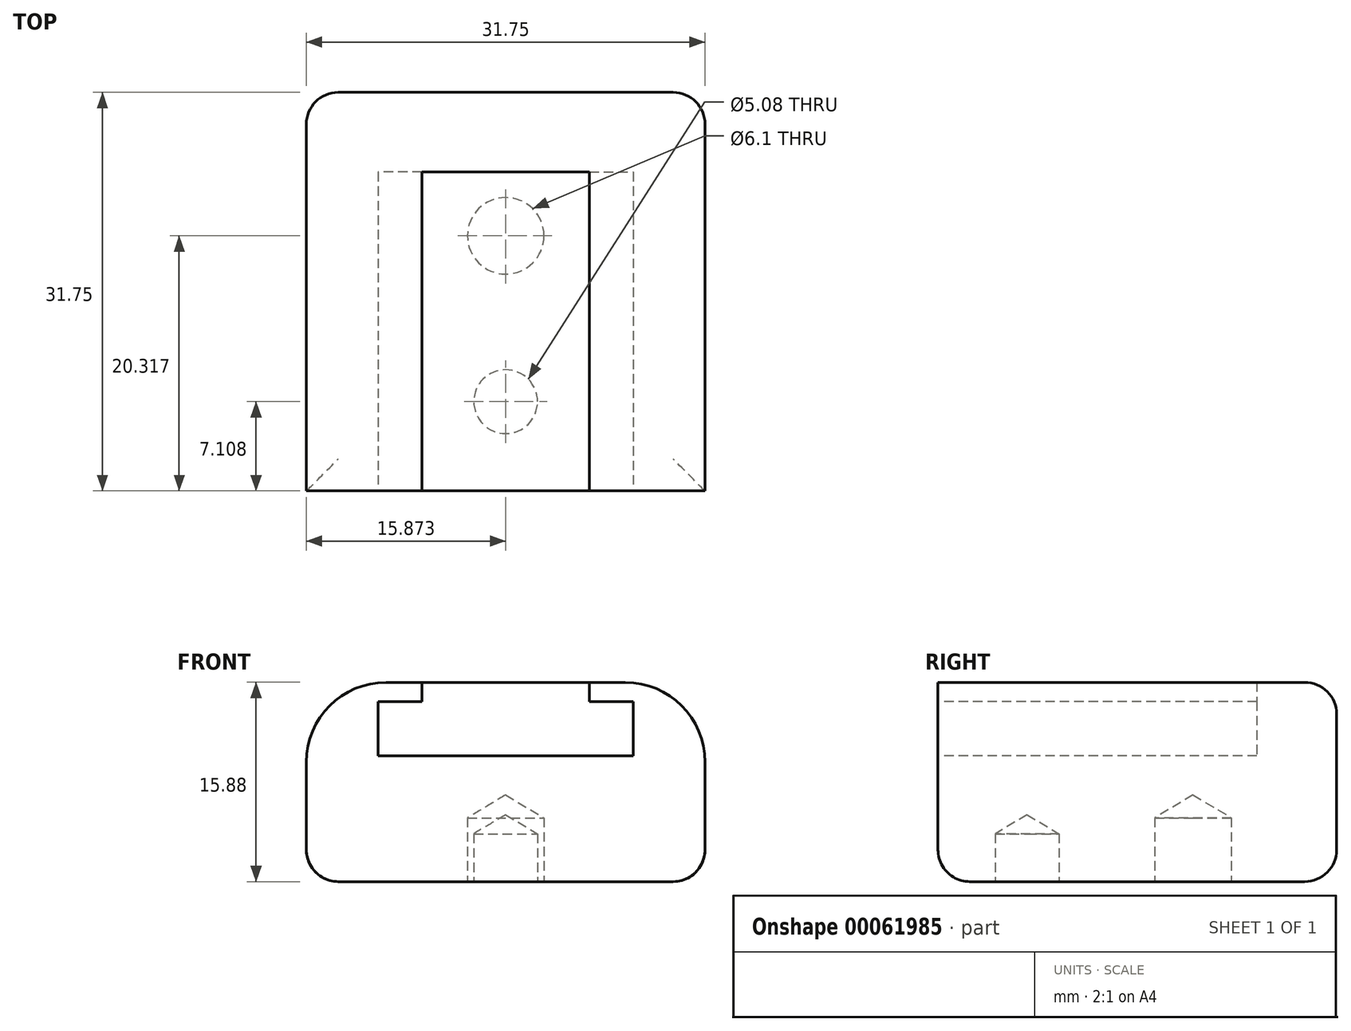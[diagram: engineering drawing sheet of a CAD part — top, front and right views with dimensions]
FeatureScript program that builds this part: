
annotation { "Feature Type Name" : "Feature", "Feature Type Description" : "" }
export const myFeature = defineFeature(function(context is Context, id is Id, definition is map)
    precondition{}
    {
        {
            var Q0;
            Q0=qCreatedBy(makeId("Top.planeOp"),FACE);
            var sketch = newSketch(context, id + "F0", { "sketchPlane" : qUnion([Q0])});
            skLineSegment(sketch, "E0.bottom", {"start": v(-42.71, 6.59) * mm, "end": v(-10.96, 6.59) * mm});
            skLineSegment(sketch, "E0.top", {"start": v(-42.71, -25.16) * mm, "end": v(-10.96, -25.16) * mm});
            skLineSegment(sketch, "E0.left", {"start": v(-42.71, 6.59) * mm, "end": v(-42.71, -25.16) * mm});
            skLineSegment(sketch, "E0.right", {"start": v(-10.96, 6.59) * mm, "end": v(-10.96, -25.16) * mm});
            skSolve(sketch);
        }
        {
            var Q0;
            Q0 = qSketchRegion(id + "F0", true);
            extrude(context, id + "F1", {"entities" : qUnion([Q0]), "depth" : 15.88 * mm});
        }
        {
            var Q0;
            Q0=makeQuery(id+"F1.opExtrude","SWEPT_FACE",FACE,{"disambiguationData":[OSD([sQuery(id+"F0.wireOp",EDGE,"E0.top")])]});
            var sketch = newSketch(context, id + "F2", { "sketchPlane" : qUnion([Q0])});
            skLineSegment(sketch, "E1", {"start": v(-33.5, 15.88) * mm, "end": v(-33.5, 14.35) * mm});
            skLineSegment(sketch, "E2", {"start": v(-33.5, 14.35) * mm, "end": v(-37, 14.35) * mm});
            skLineSegment(sketch, "E3", {"start": v(-37, 14.35) * mm, "end": v(-37, 10.03) * mm});
            skLineSegment(sketch, "E4", {"start": v(-37, 10.03) * mm, "end": v(-16.68, 10.03) * mm});
            skLineSegment(sketch, "E5", {"start": v(-16.68, 10.03) * mm, "end": v(-16.68, 14.35) * mm});
            skLineSegment(sketch, "E6", {"start": v(-16.68, 14.35) * mm, "end": v(-20.17, 14.35) * mm});
            skLineSegment(sketch, "E7", {"start": v(-20.17, 14.35) * mm, "end": v(-20.17, 15.88) * mm});
            skLineSegment(sketch, "E8", {"start": v(-20.17, 15.88) * mm, "end": v(-33.5, 15.88) * mm});
            skSolve(sketch);
        }
        {
            var Q0;
            Q0=makeQuery(id+"F2.imprint","IMPRINT",FACE,{"disambiguationData":[TD([[makeQuery(id+"F2.imprint","IMPRINT",EDGE,{"derivedFrom":sQuery(id+"F2.wireOp",EDGE,"E1")}),1.0]])]});
            extrude(context, id + "F3", {"entities" : qUnion([Q0]), "operationType" : NewBodyOperationType.REMOVE, "oppositeDirection" : true, "depth" : 25.4 * mm});
        }
        {
            var Q0;
            Q0=makeQuery(id+"F0.imprint","IMPRINT",FACE,{"disambiguationData":[TD([[makeQuery(id+"F0.imprint","IMPRINT",EDGE,{"derivedFrom":sQuery(id+"F0.wireOp",EDGE,"E0.bottom")}),-1.0]])]});
            var sketch = newSketch(context, id + "F4", { "sketchPlane" : qUnion([Q0])});
            skCircle(sketch, "E9", {"center": v(-26.84, -18.05) * mm, "radius": 2.54 * mm});
            skSolve(sketch);
        }
        {
            var Q0;
            Q0=sQuery(id+"F4.wireOp",VERTEX,"E9.center");
            var Q1;
            Q1=makeQuery(id+"F1.opExtrude","SWEPT_BODY",BODY,{"disambiguationData":[OSD([sQuery(id+"F0.wireOp",EDGE,"E0.bottom"),sQuery(id+"F0.wireOp",EDGE,"E0.top"),sQuery(id+"F0.wireOp",EDGE,"E0.left"),sQuery(id+"F0.wireOp",EDGE,"E0.right")])]});
            hole(context, id + "F5", {"style" : HoleStyle.SIMPLE, "holeDiameter" : 5.08 * mm, "endStyle" : HoleEndStyle.BLIND, "oppositeDirection" : true, "holeDepth" : 3.8 * mm, "locations" : qUnion([Q0]), "scope" : qUnion([Q1])});
        }
        {
            var Q0;
            Q0=makeQuery(id+"F0.imprint","IMPRINT",FACE,{"disambiguationData":[TD([[makeQuery(id+"F0.imprint","IMPRINT",EDGE,{"derivedFrom":sQuery(id+"F0.wireOp",EDGE,"E0.bottom")}),-1.0]])]});
            var sketch = newSketch(context, id + "F6", { "sketchPlane" : qUnion([Q0])});
            skCircle(sketch, "E10", {"center": v(-26.84, -4.84) * mm, "radius": 3.05 * mm});
            skSolve(sketch);
        }
        {
            var Q0;
            Q0=sQuery(id+"F6.wireOp",VERTEX,"E10.center");
            var Q1;
            Q1=makeQuery(id+"F1.opExtrude","SWEPT_BODY",BODY,{"disambiguationData":[OSD([sQuery(id+"F0.wireOp",EDGE,"E0.bottom"),sQuery(id+"F0.wireOp",EDGE,"E0.top"),sQuery(id+"F0.wireOp",EDGE,"E0.left"),sQuery(id+"F0.wireOp",EDGE,"E0.right")])]});
            hole(context, id + "F7", {"style" : HoleStyle.SIMPLE, "holeDiameter" : 6.1 * mm, "endStyle" : HoleEndStyle.BLIND, "oppositeDirection" : true, "holeDepth" : 5.08 * mm, "locations" : qUnion([Q0]), "scope" : qUnion([Q1])});
        }
        {
            var Q0;
            Q0=makeQuery(id+"F1.opExtrude","CAP_EDGE",EDGE,{"disambiguationData":[OSD([sQuery(id+"F0.wireOp",EDGE,"E0.left")])],"isStart":false});
            var Q1;
            Q1=makeQuery(id+"F1.opExtrude","CAP_EDGE",EDGE,{"disambiguationData":[OSD([sQuery(id+"F0.wireOp",EDGE,"E0.right")])],"isStart":false});
            fillet(context, id + "F8", {"entities" : qUnion([Q0, Q1]), "radius" : 6.35 * mm, "tangentPropagation" : true, "allowEdgeOverflow" : false});
        }
        {
            var Q0;
            Q0=makeQuery(id+"F1.opExtrude","CAP_EDGE",EDGE,{"disambiguationData":[OSD([sQuery(id+"F0.wireOp",EDGE,"E0.left")])],"isStart":true});
            var Q1;
            Q1=makeQuery(id+"F1.opExtrude","CAP_EDGE",EDGE,{"disambiguationData":[OSD([sQuery(id+"F0.wireOp",EDGE,"E0.right")])],"isStart":true});
            var Q2;
            Q2=makeQuery(id+"F1.opExtrude","CAP_EDGE",EDGE,{"disambiguationData":[OSD([sQuery(id+"F0.wireOp",EDGE,"E0.top")])],"isStart":true});
            var Q3;
            Q3=makeQuery(id+"F1.opExtrude","CAP_EDGE",EDGE,{"disambiguationData":[OSD([sQuery(id+"F0.wireOp",EDGE,"E0.bottom")])],"isStart":true});
            var Q4;
            Q4=makeQuery(id+"F1.opExtrude","CAP_EDGE",EDGE,{"disambiguationData":[OSD([sQuery(id+"F0.wireOp",EDGE,"E0.bottom")])],"isStart":false});
            fillet(context, id + "F9", {"entities" : qUnion([Q0, Q1, Q2, Q3, Q4]), "radius" : 2.54 * mm, "tangentPropagation" : true, "allowEdgeOverflow" : false});
        }
    });
